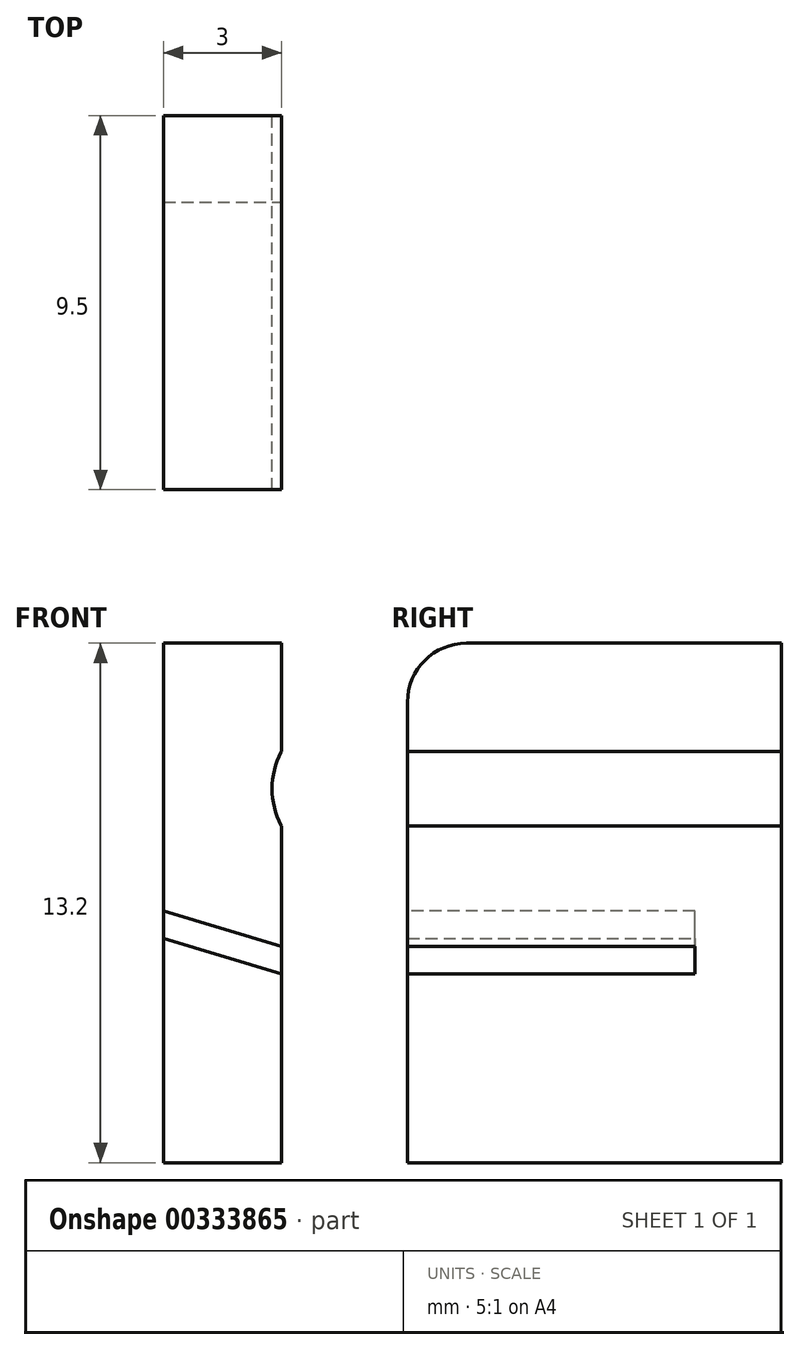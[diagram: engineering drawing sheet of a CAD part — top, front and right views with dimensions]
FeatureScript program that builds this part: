
annotation { "Feature Type Name" : "Feature", "Feature Type Description" : "" }
export const myFeature = defineFeature(function(context is Context, id is Id, definition is map)
    precondition{}
    {
        {
            var Q0;
            Q0=qCreatedBy(makeId("Front.planeOp"),FACE);
            var sketch = newSketch(context, id + "F0", { "sketchPlane" : qUnion([Q0])});
            skLineSegment(sketch, "E0.bottom", {"start": v(0, 0) * mm, "end": v(4, 0) * mm});
            skLineSegment(sketch, "E0.left", {"start": v(0, 0) * mm, "end": v(0, 4) * mm});
            skLineSegment(sketch, "E0.right", {"start": v(4, 0) * mm, "end": v(4, 1.55) * mm});
            skLineSegment(sketch, "E1", {"start": v(0, 2.5) * mm, "end": v(-3.1, 2.5) * mm});
            skPoint(sketch, "E2.visualSharp", {"position": v(4, 2.5) * mm});
            skLineSegment(sketch, "E3", {"start": v(4, 2.5) * mm, "end": v(3.5, 2.5) * mm});
            skLineSegment(sketch, "E4", {"start": v(4, 3.43) * mm, "end": v(4, 3.45) * mm});
            skLineSegment(sketch, "E5.MirrorCS", {"start": v(4, 1.57) * mm, "end": v(4, 1.55) * mm});
            skPoint(sketch, "E6.visualSharp", {"position": v(3.5, 2.5) * mm});
            skArc(sketch, "E6.filletArc", {"start": v(4, 3.43) * mm, "mid": v(3.76, 2.5) * mm, "end": v(4, 1.57) * mm});
            skPoint(sketch, "E7.orphan", {"position": v(5.5, -1.3) * mm});
            skPoint(sketch, "E8.end.orphan", {"position": v(5.5, 6.3) * mm});
            skLineSegment(sketch, "E9", {"start": v(-1, 4) * mm, "end": v(-1, 0) * mm});
            skLineSegment(sketch, "E10", {"start": v(-1, 0) * mm, "end": v(0, 0) * mm});
            skLineSegment(sketch, "E11", {"start": v(4, 1.55) * mm, "end": v(4, -1.5) * mm});
            skLineSegment(sketch, "E12", {"start": v(4, -1.5) * mm, "end": v(-1, 0) * mm});
            skLineSegment(sketch, "E13.top", {"start": v(4, 4) * mm, "end": v(-1, 4) * mm});
            skPoint(sketch, "E14.orphan", {"position": v(4, 5) * mm});
            skPoint(sketch, "E15.orphan", {"position": v(0, 5) * mm});
            skLineSegment(sketch, "E16.trimOffspring", {"start": v(4, 3.45) * mm, "end": v(4, 4) * mm});
            skSolve(sketch);
        }
        {
            var Q0;
            Q0 = qSketchRegion(id + "F0", true);
            extrude(context, id + "F1", {"entities" : qUnion([Q0]), "depth" : 10 * mm});
        }
        {
            var Q0;
            Q0=makeQuery(id+"F1.opExtrude","SWEPT_FACE",FACE,{"disambiguationData":[OSD([sQuery(id+"F0.wireOp",EDGE,"E13.top")])]});
            cPlane(context, id + "F2", {"entities" : qUnion([Q0]), "cplaneType" : CPlaneType.OFFSET, "offset" : 3 * mm, "oppositeDirection" : true, "width" : 150 * mm, "height" : 150 * mm});
        }
        {
            var Q0;
            Q0=qCreatedBy(id+"F2.planeOp",FACE);
            var sketch = newSketch(context, id + "F3", { "sketchPlane" : qUnion([Q0])});
            skLineSegment(sketch, "E17.bottom", {"start": v(0, 0) * mm, "end": v(4, 0) * mm});
            skLineSegment(sketch, "E17.top", {"start": v(0, -2.7) * mm, "end": v(4, -2.7) * mm});
            skLineSegment(sketch, "E17.left", {"start": v(0, 0) * mm, "end": v(0, -2.7) * mm});
            skLineSegment(sketch, "E17.right", {"start": v(4, 0) * mm, "end": v(4, -2.7) * mm});
            skLineSegment(sketch, "E18.bottom", {"start": v(0, 0) * mm, "end": v(-1, 0) * mm});
            skLineSegment(sketch, "E18.top", {"start": v(0, -2.7) * mm, "end": v(-1, -2.7) * mm});
            skLineSegment(sketch, "E18.right", {"start": v(-1, 0) * mm, "end": v(-1, -2.7) * mm});
            skSolve(sketch);
        }
        {
            var Q0;
            Q0 = qSketchRegion(id + "F3", true);
            extrude(context, id + "F4", {"entities" : qUnion([Q0]), "operationType" : NewBodyOperationType.ADD, "oppositeDirection" : true, "depth" : 7 * mm});
        }
        {
            var Q0;
            Q0=makeQuery(id+"F4.opExtrude","SWEPT_FACE",FACE,{"disambiguationData":[OSD([sQuery(id+"F3.wireOp",EDGE,"E17.top"),sQuery(id+"F3.wireOp",EDGE,"E18.top")])]});
            var sketch = newSketch(context, id + "F5", { "sketchPlane" : qUnion([Q0])});
            skLineSegment(sketch, "E19", {"start": v(4, -6) * mm, "end": v(4, -2.2) * mm});
            skLineSegment(sketch, "E20", {"start": v(-1, -6) * mm, "end": v(-1, -0.7) * mm});
            skLineSegment(sketch, "E21", {"start": v(-1, -0.7) * mm, "end": v(4, -2.2) * mm});
            skLineSegment(sketch, "E22", {"start": v(-1, -6) * mm, "end": v(4, -6) * mm});
            skSolve(sketch);
        }
        {
            var Q0;
            Q0 = qSketchRegion(id + "F5", true);
            var Q1;
            Q1=makeQuery(id+"F1.opExtrude","CAP_FACE",FACE,{"disambiguationData":[OSD([sQuery(id+"F0.wireOp",EDGE,"E4"),sQuery(id+"F0.wireOp",EDGE,"E5.MirrorCS"),sQuery(id+"F0.wireOp",EDGE,"E6.filletArc"),sQuery(id+"F0.wireOp",EDGE,"E9"),sQuery(id+"F0.wireOp",EDGE,"E11"),sQuery(id+"F0.wireOp",EDGE,"E12"),sQuery(id+"F0.wireOp",EDGE,"E13.top"),sQuery(id+"F0.wireOp",EDGE,"E16.trimOffspring")])],"isStart":false});
            extrude(context, id + "F6", {"entities" : qUnion([Q0]), "operationType" : NewBodyOperationType.ADD, "endBound" : BoundingType.UP_TO_SURFACE, "endBoundEntityFace" : qUnion([Q1]), "depth" : 25 * mm});
        }
        {
            var Q0;
            Q0=makeQuery(id+"F6.boolean.opBoolean","MERGE",FACE,{"derivedFrom":[makeQuery(id+"F4.opExtrude","CAP_FACE",FACE,{"disambiguationData":[OSD([sQuery(id+"F3.wireOp",EDGE,"E17.bottom"),sQuery(id+"F3.wireOp",EDGE,"E17.top"),sQuery(id+"F3.wireOp",EDGE,"E17.right"),sQuery(id+"F3.wireOp",EDGE,"E18.bottom"),sQuery(id+"F3.wireOp",EDGE,"E18.top"),sQuery(id+"F3.wireOp",EDGE,"E18.right")])],"isStart":false}),makeQuery(id+"F6.opExtrude","SWEPT_FACE",FACE,{"disambiguationData":[OSD([sQuery(id+"F5.wireOp",EDGE,"E22")])]})]});
            extrude(context, id + "F7", {"entities" : qUnion([Q0]), "operationType" : NewBodyOperationType.ADD, "depth" : 1 * mm});
        }
        {
            var Q0;
            Q0=makeQuery(id+"F1.opExtrude","SWEPT_FACE",FACE,{"disambiguationData":[OSD([sQuery(id+"F0.wireOp",EDGE,"E13.top")])]});
            extrude(context, id + "F8", {"entities" : qUnion([Q0]), "operationType" : NewBodyOperationType.ADD, "depth" : 0.5 * mm});
        }
        {
            var Q0;
            {var subQ0=sQuery(id+"F0.wireOp",EDGE,"E13.top");var subQ1=sQuery(id+"F3.wireOp",EDGE,"E18.bottom");var subQ2=sQuery(id+"F3.wireOp",EDGE,"E17.bottom");Q0=makeQuery(id+"F8.boolean.opBoolean","MERGE",FACE,{"derivedFrom":[makeQuery(id+"F7.boolean.opBoolean","MERGE",FACE,{"derivedFrom":[makeQuery(id+"F4.boolean.opBoolean","MERGE",FACE,{"derivedFrom":[makeQuery(id+"F1.opExtrude","CAP_FACE",FACE,{"disambiguationData":[OSD([sQuery(id+"F0.wireOp",EDGE,"E4"),sQuery(id+"F0.wireOp",EDGE,"E5.MirrorCS"),sQuery(id+"F0.wireOp",EDGE,"E6.filletArc"),sQuery(id+"F0.wireOp",EDGE,"E9"),sQuery(id+"F0.wireOp",EDGE,"E11"),sQuery(id+"F0.wireOp",EDGE,"E12"),subQ0,sQuery(id+"F0.wireOp",EDGE,"E16.trimOffspring")])],"isStart":true}),makeQuery(id+"F4.opExtrude","SWEPT_FACE",FACE,{"disambiguationData":[OSD([subQ2,subQ1])]})]}),makeQuery(id+"F7.opExtrude","SWEPT_FACE",FACE,{"disambiguationData":[OSD([subQ2,subQ1])]})]}),makeQuery(id+"F8.opExtrude","SWEPT_FACE",FACE,{"disambiguationData":[OSD([subQ0]),TDD([makeQuery(id+"F1.opExtrude","CAP_EDGE",EDGE,{"disambiguationData":[OSD([subQ0])],"isStart":true})])]})]});}
            extrude(context, id + "F9", {"entities" : qUnion([Q0]), "operationType" : NewBodyOperationType.REMOVE, "oppositeDirection" : true, "depth" : 0.5 * mm});
        }
        {
            var Q0;
            Q0=makeQuery(id+"F8.opExtrude","CAP_FACE",FACE,{"disambiguationData":[OSD([sQuery(id+"F0.wireOp",EDGE,"E13.top")])],"isStart":false});
            extrude(context, id + "F10", {"entities" : qUnion([Q0]), "operationType" : NewBodyOperationType.ADD, "depth" : 0.5 * mm});
        }
        {
            var Q0;
            {var subQ0=sQuery(id+"F5.wireOp",EDGE,"E22");var subQ1=sQuery(id+"F0.wireOp",EDGE,"E16.trimOffspring");var subQ2=sQuery(id+"F0.wireOp",EDGE,"E13.top");var subQ3=sQuery(id+"F0.wireOp",EDGE,"E12");var subQ4=sQuery(id+"F0.wireOp",EDGE,"E11");var subQ5=sQuery(id+"F0.wireOp",EDGE,"E9");var subQ6=sQuery(id+"F0.wireOp",EDGE,"E6.filletArc");var subQ7=sQuery(id+"F0.wireOp",EDGE,"E5.MirrorCS");var subQ8=sQuery(id+"F0.wireOp",EDGE,"E4");Q0=makeQuery(id+"FcvEmVvv3j6Bp3b_1.boolean.opBoolean","MERGE",FACE,{"derivedFrom":[makeQuery(id+"F7.boolean.opBoolean","MERGE",FACE,{"derivedFrom":[makeQuery(id+"F6.opExtrude","CAP_FACE",FACE,{"disambiguationData":[OSD([subQ8,subQ7,subQ6,subQ5,subQ4,subQ3,subQ2,subQ1])],"isStart":false}),makeQuery(id+"F7.opExtrude","SWEPT_FACE",FACE,{"disambiguationData":[OSD([subQ8,subQ7,subQ6,subQ5,subQ4,subQ3,subQ2,subQ1,subQ0])]})]}),makeQuery(id+"FcvEmVvv3j6Bp3b_1.opExtrude","SWEPT_FACE",FACE,{"disambiguationData":[OSD([subQ8,subQ7,subQ6,subQ5,subQ4,subQ3,subQ2,subQ1,subQ0])]})]});}
            var sketch = newSketch(context, id + "F11", { "sketchPlane" : qUnion([Q0])});
            skLineSegment(sketch, "E23.bottom", {"start": v(-1, -8) * mm, "end": v(1, -8) * mm});
            skLineSegment(sketch, "E23.top", {"start": v(-1, 6.98) * mm, "end": v(1, 6.98) * mm});
            skLineSegment(sketch, "E23.left", {"start": v(-1, -8) * mm, "end": v(-1, 6.98) * mm});
            skLineSegment(sketch, "E23.right", {"start": v(1, -8) * mm, "end": v(1, 6.98) * mm});
            skSolve(sketch);
        }
        {
            var Q0;
            Q0 = qSketchRegion(id + "F11", true);
            extrude(context, id + "F12", {"entities" : qUnion([Q0]), "operationType" : NewBodyOperationType.REMOVE, "oppositeDirection" : true, "depth" : 25 * mm});
        }
        {
            var Q0;
            Q0=makeQuery(id+"F10.opExtrude","CAP_FACE",FACE,{"disambiguationData":[OSD([sQuery(id+"F0.wireOp",EDGE,"E13.top")])],"isStart":false});
            extrude(context, id + "F13", {"entities" : qUnion([Q0]), "operationType" : NewBodyOperationType.ADD, "depth" : 1.2 * mm});
        }
        {
            var Q0;
            {var subQ0=sQuery(id+"F0.wireOp",EDGE,"E13.top");Q0=makeQuery(id+"F13.opExtrude","CAP_EDGE",EDGE,{"disambiguationData":[OSD([subQ0]),TDD([makeQuery(id+"F10.opExtrude","CAP_EDGE",EDGE,{"disambiguationData":[OSD([subQ0]),TDD([makeQuery(id+"F8.opExtrude","CAP_EDGE",EDGE,{"disambiguationData":[OSD([subQ0]),TDD([makeQuery(id+"F1.opExtrude","CAP_EDGE",EDGE,{"disambiguationData":[OSD([subQ0])],"isStart":false})])],"isStart":false})])],"isStart":false})])],"isStart":false});}
            var Q1;
            {var subQ0=sQuery(id+"F0.wireOp",EDGE,"E13.top");Q1=makeQuery(id+"F13.opExtrude","CAP_EDGE",EDGE,{"disambiguationData":[OSD([subQ0]),TDD([makeQuery(id+"F10.opExtrude","CAP_EDGE",EDGE,{"disambiguationData":[OSD([subQ0]),TDD([makeQuery(id+"F9.boolean.opBoolean","COPY",EDGE,{"derivedFrom":makeQuery(id+"F9.opExtrude","CAP_EDGE",EDGE,{"disambiguationData":[OSD([subQ0])],"isStart":false})})])],"isStart":false})])],"isStart":false});}
            fillet(context, id + "F14", {"entities" : qUnion([Q0, Q1]), "radius" : 1.5 * mm, "tangentPropagation" : true, "allowEdgeOverflow" : false});
        }
    });
